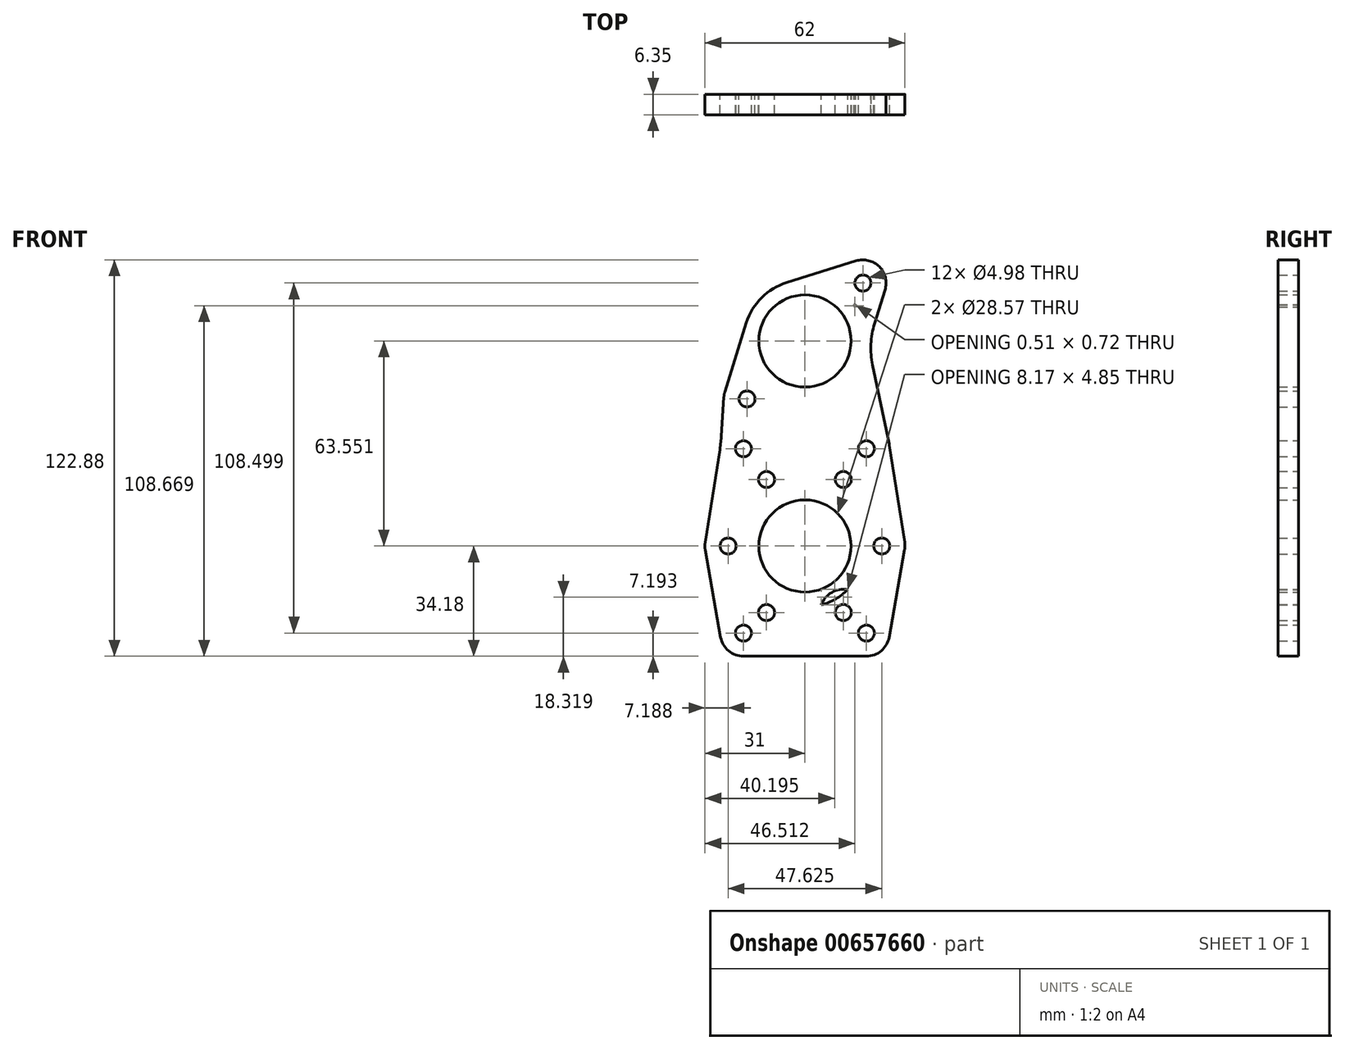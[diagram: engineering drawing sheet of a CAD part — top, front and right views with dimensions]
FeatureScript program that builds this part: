
annotation { "Feature Type Name" : "Feature", "Feature Type Description" : "" }
export const myFeature = defineFeature(function(context is Context, id is Id, definition is map)
    precondition{}
    {
        {
            var Q0;
            Q0=qCreatedBy(makeId("Front.planeOp"),FACE);
            var sketch = newSketch(context, id + "F0", { "sketchPlane" : qUnion([Q0])});
            skLineSegment(sketch, "E0.bottom", {"start": v(0, 0) * mm, "end": v(76.2, 0) * mm});
            skLineSegment(sketch, "E0.top", {"start": v(0, 127) * mm, "end": v(76.2, 127) * mm});
            skLineSegment(sketch, "E0.left", {"start": v(0, 0) * mm, "end": v(0, 127) * mm});
            skLineSegment(sketch, "E0.right", {"start": v(76.2, 0) * mm, "end": v(76.2, 127) * mm});
            skCircle(sketch, "E1", {"center": v(38.1, 38.1) * mm, "radius": 14.29 * mm});
            skCircle(sketch, "E2", {"center": v(38.1, 38.1) * mm, "radius": 23.81 * mm, "construction": true});
            skLineSegment(sketch, "E3", {"start": v(38.1, 38.1) * mm, "end": v(14.29, 38.1) * mm});
            skCircle(sketch, "E4", {"center": v(14.29, 38.1) * mm, "radius": 2.49 * mm});
            skCircle(sketch, "E5.1.0", {"center": v(26.2, 17.48) * mm, "radius": 2.49 * mm});
            skCircle(sketch, "E5.2.0", {"center": v(50, 17.48) * mm, "radius": 2.49 * mm});
            skCircle(sketch, "E5.3.0", {"center": v(61.91, 38.1) * mm, "radius": 2.49 * mm});
            skCircle(sketch, "E5.4.0", {"center": v(50, 58.72) * mm, "radius": 2.49 * mm});
            skCircle(sketch, "E5.5.0", {"center": v(26.2, 58.72) * mm, "radius": 2.49 * mm});
            skLineSegment(sketch, "E6.bottom", {"start": v(19.05, 68.26) * mm, "end": v(57.15, 68.26) * mm, "construction": true});
            skLineSegment(sketch, "E6.top", {"start": v(19.05, 11.11) * mm, "end": v(57.15, 11.11) * mm, "construction": true});
            skLineSegment(sketch, "E6.left", {"start": v(19.05, 68.26) * mm, "end": v(19.05, 11.11) * mm, "construction": true});
            skLineSegment(sketch, "E6.right", {"start": v(57.15, 68.26) * mm, "end": v(57.15, 11.11) * mm, "construction": true});
            skCircle(sketch, "E7", {"center": v(19.05, 68.26) * mm, "radius": 2.49 * mm});
            skCircle(sketch, "E8", {"center": v(57.15, 68.26) * mm, "radius": 2.49 * mm});
            skCircle(sketch, "E9", {"center": v(57.15, 11.11) * mm, "radius": 2.49 * mm});
            skCircle(sketch, "E10", {"center": v(19.05, 11.11) * mm, "radius": 2.49 * mm});
            skCircle(sketch, "E11", {"center": v(38.1, 101.65) * mm, "radius": 14.29 * mm});
            skCircle(sketch, "E12", {"center": v(38.1, 101.65) * mm, "radius": 25.4 * mm, "construction": true});
            skCircle(sketch, "E13", {"center": v(56.06, 119.61) * mm, "radius": 2.49 * mm});
            skLineSegment(sketch, "E14", {"start": v(38.1, 101.65) * mm, "end": v(56.06, 119.61) * mm});
            skLineSegment(sketch, "E15", {"start": v(38.1, 101.65) * mm, "end": v(63.5, 101.65) * mm});
            skCircle(sketch, "E16.1.0", {"center": v(20.14, 83.7) * mm, "radius": 2.49 * mm});
            skLineSegment(sketch, "E16.1.1", {"start": v(76.2, 203.3) * mm, "end": v(76.2, 76.3) * mm});
            skCircle(sketch, "E17", {"center": v(19.05, 11.11) * mm, "radius": 7.19 * mm});
            skCircle(sketch, "E18", {"center": v(57.15, 11.11) * mm, "radius": 7.19 * mm});
            skCircle(sketch, "E19", {"center": v(57.15, 68.26) * mm, "radius": 7.19 * mm});
            skCircle(sketch, "E20", {"center": v(19.05, 68.26) * mm, "radius": 7.19 * mm});
            skCircle(sketch, "E21", {"center": v(14.29, 38.1) * mm, "radius": 7.19 * mm});
            skCircle(sketch, "E22", {"center": v(61.91, 38.1) * mm, "radius": 7.19 * mm});
            skCircle(sketch, "E23", {"center": v(38.1, 38.1) * mm, "radius": 18.99 * mm});
            skLineSegment(sketch, "E24", {"start": v(15.67, 61.92) * mm, "end": v(20.31, 61.19) * mm, "construction": true});
            skLineSegment(sketch, "E25", {"start": v(20.31, 61.19) * mm, "end": v(17.67, 44.44) * mm});
            skLineSegment(sketch, "E26", {"start": v(15.67, 61.92) * mm, "end": v(13.03, 45.18) * mm});
            skLineSegment(sketch, "E27", {"start": v(55.89, 61.19) * mm, "end": v(58.53, 44.44) * mm});
            skLineSegment(sketch, "E28", {"start": v(58.53, 44.44) * mm, "end": v(63.17, 45.18) * mm, "construction": true});
            skLineSegment(sketch, "E29", {"start": v(63.17, 45.18) * mm, "end": v(60.53, 61.92) * mm});
            skLineSegment(sketch, "E30", {"start": v(25.84, 13.46) * mm, "end": v(50.36, 13.46) * mm});
            skLineSegment(sketch, "E31", {"start": v(25.84, 8.76) * mm, "end": v(50.36, 8.76) * mm});
            skCircle(sketch, "E32", {"center": v(26.2, 17.48) * mm, "radius": 7.19 * mm});
            skCircle(sketch, "E33", {"center": v(50, 17.48) * mm, "radius": 7.19 * mm});
            skCircle(sketch, "E34", {"center": v(26.2, 58.72) * mm, "radius": 7.19 * mm});
            skCircle(sketch, "E35", {"center": v(50, 58.72) * mm, "radius": 7.19 * mm});
            skLineSegment(sketch, "E36", {"start": v(15.56, 17.4) * mm, "end": v(13.15, 31) * mm});
            skLineSegment(sketch, "E37", {"start": v(13.15, 31) * mm, "end": v(17.78, 31.82) * mm, "construction": true});
            skLineSegment(sketch, "E38", {"start": v(17.78, 31.82) * mm, "end": v(20.18, 18.21) * mm});
            skLineSegment(sketch, "E39", {"start": v(63.05, 31) * mm, "end": v(60.64, 17.4) * mm});
            skLineSegment(sketch, "E40", {"start": v(60.64, 17.4) * mm, "end": v(56.02, 18.21) * mm, "construction": true});
            skLineSegment(sketch, "E41", {"start": v(56.02, 18.21) * mm, "end": v(58.42, 31.82) * mm});
            skCircle(sketch, "E42", {"center": v(38.1, 101.65) * mm, "radius": 18.99 * mm});
            skCircle(sketch, "E43", {"center": v(20.14, 83.7) * mm, "radius": 7.19 * mm});
            skCircle(sketch, "E44", {"center": v(56.06, 119.61) * mm, "radius": 7.19 * mm});
            skLineSegment(sketch, "E45", {"start": v(17.32, 77.08) * mm, "end": v(22, 76.75) * mm, "construction": true});
            skLineSegment(sketch, "E46", {"start": v(22, 76.75) * mm, "end": v(21.87, 74.87) * mm});
            skLineSegment(sketch, "E47", {"start": v(17.32, 77.08) * mm, "end": v(17.18, 75.2) * mm});
            skLineSegment(sketch, "E48", {"start": v(35.75, 56.94) * mm, "end": v(40.45, 56.94) * mm, "construction": true});
            skLineSegment(sketch, "E49", {"start": v(40.45, 56.94) * mm, "end": v(40.45, 82.81) * mm});
            skLineSegment(sketch, "E50", {"start": v(35.75, 56.94) * mm, "end": v(35.75, 82.81) * mm});
            skLineSegment(sketch, "E51", {"start": v(51.74, 73) * mm, "end": v(45.4, 84.12) * mm});
            skLineSegment(sketch, "E52", {"start": v(45.4, 84.12) * mm, "end": v(49.48, 86.45) * mm, "construction": true});
            skLineSegment(sketch, "E53", {"start": v(49.48, 86.45) * mm, "end": v(55.82, 75.33) * mm});
            skLineSegment(sketch, "E54", {"start": v(59.35, 75.1) * mm, "end": v(58.55, 112.87) * mm});
            skLineSegment(sketch, "E55", {"start": v(58.55, 112.87) * mm, "end": v(53.86, 112.77) * mm, "construction": true});
            skLineSegment(sketch, "E56", {"start": v(53.86, 112.77) * mm, "end": v(54.66, 75) * mm});
            skLineSegment(sketch, "E57", {"start": v(32.45, 119.78) * mm, "end": v(53.92, 126.47) * mm});
            skLineSegment(sketch, "E58", {"start": v(19.97, 107.3) * mm, "end": v(13.28, 85.83) * mm});
            skLineSegment(sketch, "E59", {"start": v(12.97, 84.2) * mm, "end": v(11.88, 68.77) * mm});
            skLineSegment(sketch, "E60", {"start": v(11.95, 69.38) * mm, "end": v(7.19, 39.22) * mm});
            skLineSegment(sketch, "E61", {"start": v(7.2, 36.85) * mm, "end": v(11.97, 9.86) * mm});
            skLineSegment(sketch, "E62", {"start": v(19.05, 3.92) * mm, "end": v(57.15, 3.92) * mm});
            skLineSegment(sketch, "E63", {"start": v(64.23, 9.86) * mm, "end": v(69, 36.85) * mm});
            skLineSegment(sketch, "E64", {"start": v(69.01, 39.22) * mm, "end": v(64.25, 69.38) * mm});
            skLineSegment(sketch, "E65", {"start": v(64.19, 69.74) * mm, "end": v(56.68, 105.54) * mm});
            skLineSegment(sketch, "E66", {"start": v(56.23, 96) * mm, "end": v(62.92, 117.47) * mm});
            skSolve(sketch);
        }
        {
            var Q0;
            Q0=makeQuery(id+"F0.imprint","IMPRINT",FACE,{"disambiguationData":[TD([[makeQuery(id+"F0.imprint","IMPRINT",EDGE,{"derivedFrom":sQuery(id+"F0.wireOp",EDGE,"E16.1.0")}),-1.0]])]});
            var Q1;
            {var subQ7=sQuery(id+"F0.wireOp",EDGE,"E11");var subQ9=sQuery(id+"F0.wireOp",EDGE,"E14");var subQ10=makeQuery(id+"F0.imprint","INTERSECT",VERTEX,{"derivedFrom":[subQ7,subQ9]});Q1=makeQuery(id+"F0.imprint","IMPRINT",FACE,{"disambiguationData":[TD([[makeQuery(id+"F0.imprint","IMPRINT",EDGE,{"disambiguationData":[TD([[subQ10,-1.0]])],"derivedFrom":subQ7}),-1.0]])]});}
            var Q2;
            {var subQ0=sQuery(id+"F0.wireOp",EDGE,"E43");var subQ1=sQuery(id+"F0.wireOp",EDGE,"E42");var subQ2=makeQuery(id+"F0.imprint","INTERSECT",VERTEX,{"disambiguationData":[OD(0.0)],"derivedFrom":[subQ1,subQ0]});Q2=makeQuery(id+"F0.imprint","IMPRINT",FACE,{"disambiguationData":[TD([[makeQuery(id+"F0.imprint","IMPRINT",EDGE,{"disambiguationData":[TD([[subQ2,-1.0]])],"derivedFrom":subQ1}),1.0]])]});}
            var Q3;
            {var subQ3=sQuery(id+"F0.wireOp",EDGE,"E11");var subQ7=sQuery(id+"F0.wireOp",EDGE,"E14");var subQ9=makeQuery(id+"F0.imprint","INTERSECT",VERTEX,{"derivedFrom":[subQ3,subQ7]});Q3=makeQuery(id+"F0.imprint","IMPRINT",FACE,{"disambiguationData":[TD([[makeQuery(id+"F0.imprint","IMPRINT",EDGE,{"disambiguationData":[TD([[subQ9,1.0]])],"derivedFrom":subQ3}),-1.0]])]});}
            var Q4;
            {var subQ0=sQuery(id+"F0.wireOp",EDGE,"E42");var subQ1=sQuery(id+"F0.wireOp",EDGE,"E14");var subQ2=makeQuery(id+"F0.imprint","INTERSECT",VERTEX,{"derivedFrom":[subQ1,subQ0]});Q4=makeQuery(id+"F0.imprint","IMPRINT",FACE,{"disambiguationData":[TD([[makeQuery(id+"F0.imprint","IMPRINT",EDGE,{"disambiguationData":[TD([[subQ2,1.0]])],"derivedFrom":subQ1}),1.0]])]});}
            var Q5;
            {var subQ0=sQuery(id+"F0.wireOp",EDGE,"E42");var subQ1=sQuery(id+"F0.wireOp",EDGE,"E14");var subQ2=makeQuery(id+"F0.imprint","INTERSECT",VERTEX,{"derivedFrom":[subQ1,subQ0]});Q5=makeQuery(id+"F0.imprint","IMPRINT",FACE,{"disambiguationData":[TD([[makeQuery(id+"F0.imprint","IMPRINT",EDGE,{"disambiguationData":[TD([[subQ2,1.0]])],"derivedFrom":subQ1}),-1.0]])]});}
            var Q6;
            Q6=makeQuery(id+"F0.imprint","IMPRINT",FACE,{"disambiguationData":[TD([[makeQuery(id+"F0.imprint","IMPRINT",EDGE,{"derivedFrom":sQuery(id+"F0.wireOp",EDGE,"E13")}),-1.0]])]});
            var Q7;
            {var subQ0=sQuery(id+"F0.wireOp",EDGE,"E46");Q7=makeQuery(id+"F0.imprint","IMPRINT",FACE,{"disambiguationData":[TD([[makeQuery(id+"F0.imprint","IMPRINT",EDGE,{"derivedFrom":subQ0}),-1.0]])]});}
            var Q8;
            Q8=makeQuery(id+"F0.imprint","IMPRINT",FACE,{"disambiguationData":[TD([[makeQuery(id+"F0.imprint","IMPRINT",EDGE,{"derivedFrom":sQuery(id+"F0.wireOp",EDGE,"E7")}),-1.0]])]});
            var Q9;
            {var subQ0=sQuery(id+"F0.wireOp",EDGE,"E20");var subQ1=makeQuery(id+"F0.imprint","INTERSECT",VERTEX,{"derivedFrom":[subQ0,sQuery(id+"F0.wireOp",EDGE,"E25")]});Q9=makeQuery(id+"F0.imprint","IMPRINT",FACE,{"disambiguationData":[TD([[makeQuery(id+"F0.imprint","IMPRINT",EDGE,{"disambiguationData":[TD([[subQ1,1.0]])],"derivedFrom":subQ0}),1.0]])]});}
            var Q10;
            Q10=makeQuery(id+"F0.imprint","IMPRINT",FACE,{"disambiguationData":[TD([[makeQuery(id+"F0.imprint","IMPRINT",EDGE,{"derivedFrom":sQuery(id+"F0.wireOp",EDGE,"E5.5.0")}),-1.0]])]});
            var Q11;
            Q11=makeQuery(id+"F0.imprint","IMPRINT",FACE,{"disambiguationData":[TD([[makeQuery(id+"F0.imprint","IMPRINT",EDGE,{"derivedFrom":sQuery(id+"F0.wireOp",EDGE,"E8")}),-1.0]])]});
            var Q12;
            {var subQ0=sQuery(id+"F0.wireOp",EDGE,"E29");Q12=makeQuery(id+"F0.imprint","IMPRINT",FACE,{"disambiguationData":[TD([[makeQuery(id+"F0.imprint","IMPRINT",EDGE,{"derivedFrom":subQ0}),1.0]])]});}
            var Q13;
            Q13=makeQuery(id+"F0.imprint","IMPRINT",FACE,{"disambiguationData":[TD([[makeQuery(id+"F0.imprint","IMPRINT",EDGE,{"derivedFrom":sQuery(id+"F0.wireOp",EDGE,"E5.3.0")}),-1.0]])]});
            var Q14;
            Q14=makeQuery(id+"F0.imprint","IMPRINT",FACE,{"disambiguationData":[TD([[makeQuery(id+"F0.imprint","IMPRINT",EDGE,{"derivedFrom":sQuery(id+"F0.wireOp",EDGE,"E5.4.0")}),-1.0]])]});
            var Q15;
            Q15=makeQuery(id+"F0.imprint","IMPRINT",FACE,{"disambiguationData":[TD([[makeQuery(id+"F0.imprint","IMPRINT",EDGE,{"derivedFrom":sQuery(id+"F0.wireOp",EDGE,"E1")}),-1.0]])]});
            var Q16;
            {var subQ0=sQuery(id+"F0.wireOp",EDGE,"E19");var subQ1=makeQuery(id+"F0.imprint","INTERSECT",VERTEX,{"derivedFrom":[subQ0,sQuery(id+"F0.wireOp",EDGE,"E27")]});Q16=makeQuery(id+"F0.imprint","IMPRINT",FACE,{"disambiguationData":[TD([[makeQuery(id+"F0.imprint","IMPRINT",EDGE,{"disambiguationData":[TD([[subQ1,1.0]])],"derivedFrom":subQ0}),1.0]])]});}
            var Q17;
            {var subQ0=sQuery(id+"F0.wireOp",EDGE,"E27");var subQ1=sQuery(id+"F0.wireOp",EDGE,"E19");var subQ2=makeQuery(id+"F0.imprint","INTERSECT",VERTEX,{"derivedFrom":[subQ1,subQ0]});Q17=makeQuery(id+"F0.imprint","IMPRINT",FACE,{"disambiguationData":[TD([[makeQuery(id+"F0.imprint","IMPRINT",EDGE,{"disambiguationData":[TD([[subQ2,-1.0]])],"derivedFrom":subQ1}),-1.0]])]});}
            var Q18;
            {var subQ0=sQuery(id+"F0.wireOp",EDGE,"E34");var subQ1=sQuery(id+"F0.wireOp",EDGE,"E23");var subQ2=makeQuery(id+"F0.imprint","INTERSECT",VERTEX,{"disambiguationData":[OD(0.0)],"derivedFrom":[subQ1,subQ0]});Q18=makeQuery(id+"F0.imprint","IMPRINT",FACE,{"disambiguationData":[TD([[makeQuery(id+"F0.imprint","IMPRINT",EDGE,{"disambiguationData":[TD([[subQ2,-1.0]])],"derivedFrom":subQ1}),1.0]])]});}
            var Q19;
            {var subQ0=sQuery(id+"F0.wireOp",EDGE,"E26");Q19=makeQuery(id+"F0.imprint","IMPRINT",FACE,{"disambiguationData":[TD([[makeQuery(id+"F0.imprint","IMPRINT",EDGE,{"derivedFrom":subQ0}),1.0]])]});}
            var Q20;
            {var subQ0=sQuery(id+"F0.wireOp",EDGE,"E25");var subQ1=sQuery(id+"F0.wireOp",EDGE,"E20");var subQ2=makeQuery(id+"F0.imprint","INTERSECT",VERTEX,{"derivedFrom":[subQ1,subQ0]});Q20=makeQuery(id+"F0.imprint","IMPRINT",FACE,{"disambiguationData":[TD([[makeQuery(id+"F0.imprint","IMPRINT",EDGE,{"disambiguationData":[TD([[subQ2,1.0]])],"derivedFrom":subQ1}),-1.0]])]});}
            var Q21;
            {var subQ0=sQuery(id+"F0.wireOp",EDGE,"E35");var subQ1=sQuery(id+"F0.wireOp",EDGE,"E23");var subQ2=makeQuery(id+"F0.imprint","INTERSECT",VERTEX,{"disambiguationData":[OD(0.0)],"derivedFrom":[subQ1,subQ0]});Q21=makeQuery(id+"F0.imprint","IMPRINT",FACE,{"disambiguationData":[TD([[makeQuery(id+"F0.imprint","IMPRINT",EDGE,{"disambiguationData":[TD([[subQ2,-1.0]])],"derivedFrom":subQ1}),1.0]])]});}
            var Q22;
            {var subQ0=sQuery(id+"F0.wireOp",EDGE,"E23");var subQ1=sQuery(id+"F0.wireOp",EDGE,"E22");var subQ2=makeQuery(id+"F0.imprint","INTERSECT",VERTEX,{"disambiguationData":[OD(0.0)],"derivedFrom":[subQ1,subQ0]});Q22=makeQuery(id+"F0.imprint","IMPRINT",FACE,{"disambiguationData":[TD([[makeQuery(id+"F0.imprint","IMPRINT",EDGE,{"disambiguationData":[TD([[subQ2,-1.0]])],"derivedFrom":subQ1}),1.0]])]});}
            var Q23;
            Q23=makeQuery(id+"F0.imprint","IMPRINT",FACE,{"disambiguationData":[TD([[makeQuery(id+"F0.imprint","IMPRINT",EDGE,{"derivedFrom":sQuery(id+"F0.wireOp",EDGE,"E4")}),-1.0]])]});
            var Q24;
            {var subQ0=sQuery(id+"F0.wireOp",EDGE,"E36");Q24=makeQuery(id+"F0.imprint","IMPRINT",FACE,{"disambiguationData":[TD([[makeQuery(id+"F0.imprint","IMPRINT",EDGE,{"derivedFrom":subQ0}),-1.0]])]});}
            var Q25;
            {var subQ2=sQuery(id+"F0.wireOp",EDGE,"E32");var subQ6=sQuery(id+"F0.wireOp",EDGE,"E10");var subQ7=makeQuery(id+"F0.imprint","INTERSECT",VERTEX,{"disambiguationData":[OD(0.0)],"derivedFrom":[subQ6,subQ2]});Q25=makeQuery(id+"F0.imprint","IMPRINT",FACE,{"disambiguationData":[TD([[makeQuery(id+"F0.imprint","IMPRINT",EDGE,{"disambiguationData":[TD([[subQ7,-1.0]])],"derivedFrom":subQ6}),-1.0]])]});}
            var Q26;
            {var subQ0=sQuery(id+"F0.wireOp",EDGE,"E21");var subQ1=sQuery(id+"F0.wireOp",EDGE,"E3");var subQ2=makeQuery(id+"F0.imprint","INTERSECT",VERTEX,{"derivedFrom":[subQ1,subQ0]});Q26=makeQuery(id+"F0.imprint","IMPRINT",FACE,{"disambiguationData":[TD([[makeQuery(id+"F0.imprint","IMPRINT",EDGE,{"disambiguationData":[TD([[subQ2,-1.0]])],"derivedFrom":subQ1}),-1.0]])]});}
            var Q27;
            {var subQ0=sQuery(id+"F0.wireOp",EDGE,"E32");var subQ1=sQuery(id+"F0.wireOp",EDGE,"E23");var subQ2=makeQuery(id+"F0.imprint","INTERSECT",VERTEX,{"disambiguationData":[OD(0.0)],"derivedFrom":[subQ1,subQ0]});Q27=makeQuery(id+"F0.imprint","IMPRINT",FACE,{"disambiguationData":[TD([[makeQuery(id+"F0.imprint","IMPRINT",EDGE,{"disambiguationData":[TD([[subQ2,-1.0]])],"derivedFrom":subQ1}),1.0]])]});}
            var Q28;
            {var subQ0=sQuery(id+"F0.wireOp",EDGE,"E17");var subQ2=sQuery(id+"F0.wireOp",EDGE,"E5.1.0");var subQ3=makeQuery(id+"F0.imprint","INTERSECT",VERTEX,{"disambiguationData":[OD(0.0)],"derivedFrom":[subQ2,subQ0]});Q28=makeQuery(id+"F0.imprint","IMPRINT",FACE,{"disambiguationData":[TD([[makeQuery(id+"F0.imprint","IMPRINT",EDGE,{"disambiguationData":[TD([[subQ3,1.0]])],"derivedFrom":subQ2}),-1.0]])]});}
            var Q29;
            {var subQ0=sQuery(id+"F0.wireOp",EDGE,"E30");var subQ1=sQuery(id+"F0.wireOp",EDGE,"E17");var subQ2=makeQuery(id+"F0.imprint","INTERSECT",VERTEX,{"derivedFrom":[subQ1,subQ0]});Q29=makeQuery(id+"F0.imprint","IMPRINT",FACE,{"disambiguationData":[TD([[makeQuery(id+"F0.imprint","IMPRINT",EDGE,{"disambiguationData":[TD([[subQ2,1.0]])],"derivedFrom":subQ1}),-1.0]])]});}
            var Q30;
            {var subQ0=sQuery(id+"F0.wireOp",EDGE,"E38");var subQ1=sQuery(id+"F0.wireOp",EDGE,"E17");var subQ2=makeQuery(id+"F0.imprint","INTERSECT",VERTEX,{"derivedFrom":[subQ1,subQ0]});Q30=makeQuery(id+"F0.imprint","IMPRINT",FACE,{"disambiguationData":[TD([[makeQuery(id+"F0.imprint","IMPRINT",EDGE,{"disambiguationData":[TD([[subQ2,-1.0]])],"derivedFrom":subQ1}),-1.0]])]});}
            var Q31;
            {var subQ0=sQuery(id+"F0.wireOp",EDGE,"E33");var subQ1=sQuery(id+"F0.wireOp",EDGE,"E23");var subQ2=makeQuery(id+"F0.imprint","INTERSECT",VERTEX,{"disambiguationData":[OD(0.0)],"derivedFrom":[subQ1,subQ0]});Q31=makeQuery(id+"F0.imprint","IMPRINT",FACE,{"disambiguationData":[TD([[makeQuery(id+"F0.imprint","IMPRINT",EDGE,{"disambiguationData":[TD([[subQ2,-1.0]])],"derivedFrom":subQ1}),1.0]])]});}
            var Q32;
            {var subQ5=sQuery(id+"F0.wireOp",EDGE,"E18");var subQ10=sQuery(id+"F0.wireOp",EDGE,"E5.2.0");var subQ13=makeQuery(id+"F0.imprint","INTERSECT",VERTEX,{"disambiguationData":[OD(0.0)],"derivedFrom":[subQ10,subQ5]});Q32=makeQuery(id+"F0.imprint","IMPRINT",FACE,{"disambiguationData":[TD([[makeQuery(id+"F0.imprint","IMPRINT",EDGE,{"disambiguationData":[TD([[subQ13,-1.0]])],"derivedFrom":subQ10}),-1.0]])]});}
            var Q33;
            {var subQ0=sQuery(id+"F0.wireOp",EDGE,"E39");Q33=makeQuery(id+"F0.imprint","IMPRINT",FACE,{"disambiguationData":[TD([[makeQuery(id+"F0.imprint","IMPRINT",EDGE,{"derivedFrom":subQ0}),-1.0]])]});}
            var Q34;
            {var subQ0=sQuery(id+"F0.wireOp",EDGE,"E41");var subQ1=sQuery(id+"F0.wireOp",EDGE,"E18");var subQ2=makeQuery(id+"F0.imprint","INTERSECT",VERTEX,{"derivedFrom":[subQ1,subQ0]});Q34=makeQuery(id+"F0.imprint","IMPRINT",FACE,{"disambiguationData":[TD([[makeQuery(id+"F0.imprint","IMPRINT",EDGE,{"disambiguationData":[TD([[subQ2,1.0]])],"derivedFrom":subQ1}),-1.0]])]});}
            var Q35;
            {var subQ0=sQuery(id+"F0.wireOp",EDGE,"E18");var subQ2=sQuery(id+"F0.wireOp",EDGE,"E5.2.0");var subQ3=makeQuery(id+"F0.imprint","INTERSECT",VERTEX,{"disambiguationData":[OD(0.0)],"derivedFrom":[subQ2,subQ0]});Q35=makeQuery(id+"F0.imprint","IMPRINT",FACE,{"disambiguationData":[TD([[makeQuery(id+"F0.imprint","IMPRINT",EDGE,{"disambiguationData":[TD([[subQ3,1.0]])],"derivedFrom":subQ2}),-1.0]])]});}
            var Q36;
            {var subQ0=sQuery(id+"F0.wireOp",EDGE,"E30");var subQ1=sQuery(id+"F0.wireOp",EDGE,"E18");var subQ2=makeQuery(id+"F0.imprint","INTERSECT",VERTEX,{"derivedFrom":[subQ1,subQ0]});Q36=makeQuery(id+"F0.imprint","IMPRINT",FACE,{"disambiguationData":[TD([[makeQuery(id+"F0.imprint","IMPRINT",EDGE,{"disambiguationData":[TD([[subQ2,-1.0]])],"derivedFrom":subQ1}),-1.0]])]});}
            var Q37;
            {var subQ5=sQuery(id+"F0.wireOp",EDGE,"E17");var subQ10=sQuery(id+"F0.wireOp",EDGE,"E5.1.0");var subQ13=makeQuery(id+"F0.imprint","INTERSECT",VERTEX,{"disambiguationData":[OD(0.0)],"derivedFrom":[subQ10,subQ5]});Q37=makeQuery(id+"F0.imprint","IMPRINT",FACE,{"disambiguationData":[TD([[makeQuery(id+"F0.imprint","IMPRINT",EDGE,{"disambiguationData":[TD([[subQ13,-1.0]])],"derivedFrom":subQ10}),-1.0]])]});}
            var Q38;
            {var subQ0=sQuery(id+"F0.wireOp",EDGE,"E21");var subQ1=sQuery(id+"F0.wireOp",EDGE,"E3");var subQ2=makeQuery(id+"F0.imprint","INTERSECT",VERTEX,{"derivedFrom":[subQ1,subQ0]});Q38=makeQuery(id+"F0.imprint","IMPRINT",FACE,{"disambiguationData":[TD([[makeQuery(id+"F0.imprint","IMPRINT",EDGE,{"disambiguationData":[TD([[subQ2,-1.0]])],"derivedFrom":subQ1}),1.0]])]});}
            var Q39;
            {var subQ3=sQuery(id+"F0.wireOp",EDGE,"E33");var subQ6=sQuery(id+"F0.wireOp",EDGE,"E9");var subQ7=makeQuery(id+"F0.imprint","INTERSECT",VERTEX,{"disambiguationData":[OD(0.0)],"derivedFrom":[subQ6,subQ3]});Q39=makeQuery(id+"F0.imprint","IMPRINT",FACE,{"disambiguationData":[TD([[makeQuery(id+"F0.imprint","IMPRINT",EDGE,{"disambiguationData":[TD([[subQ7,-1.0]])],"derivedFrom":subQ6}),-1.0]])]});}
            var Q40;
            {var subQ5=sQuery(id+"F0.wireOp",EDGE,"E31");Q40=makeQuery(id+"F0.imprint","IMPRINT",FACE,{"disambiguationData":[TD([[makeQuery(id+"F0.imprint","IMPRINT",EDGE,{"derivedFrom":subQ5}),1.0]])]});}
            var Q41;
            {var subQ0=sQuery(id+"F0.wireOp",EDGE,"E56");var subQ1=sQuery(id+"F0.wireOp",EDGE,"E15");var subQ2=makeQuery(id+"F0.imprint","INTERSECT",VERTEX,{"derivedFrom":[subQ1,subQ0]});Q41=makeQuery(id+"F0.imprint","IMPRINT",FACE,{"disambiguationData":[TD([[makeQuery(id+"F0.imprint","IMPRINT",EDGE,{"disambiguationData":[TD([[subQ2,-1.0]])],"derivedFrom":subQ1}),1.0]])]});}
            var Q42;
            {var subQ0=sQuery(id+"F0.wireOp",EDGE,"E56");var subQ1=sQuery(id+"F0.wireOp",EDGE,"E42");var subQ2=makeQuery(id+"F0.imprint","INTERSECT",VERTEX,{"disambiguationData":[OD(0.0)],"derivedFrom":[subQ1,subQ0]});Q42=makeQuery(id+"F0.imprint","IMPRINT",FACE,{"disambiguationData":[TD([[makeQuery(id+"F0.imprint","IMPRINT",EDGE,{"disambiguationData":[TD([[subQ2,-1.0]])],"derivedFrom":subQ1}),-1.0]])]});}
            var Q43;
            {var subQ0=sQuery(id+"F0.wireOp",EDGE,"E49");Q43=makeQuery(id+"F0.imprint","IMPRINT",FACE,{"disambiguationData":[TD([[makeQuery(id+"F0.imprint","IMPRINT",EDGE,{"derivedFrom":subQ0}),1.0]])]});}
            var Q44;
            {var subQ5=sQuery(id+"F0.wireOp",EDGE,"E51");Q44=makeQuery(id+"F0.imprint","IMPRINT",FACE,{"disambiguationData":[TD([[makeQuery(id+"F0.imprint","IMPRINT",EDGE,{"derivedFrom":subQ5}),-1.0]])]});}
            var Q45;
            {var subQ0=sQuery(id+"F0.wireOp",EDGE,"E53");var subQ1=sQuery(id+"F0.wireOp",EDGE,"E19");var subQ2=makeQuery(id+"F0.imprint","INTERSECT",VERTEX,{"derivedFrom":[subQ1,subQ0]});Q45=makeQuery(id+"F0.imprint","IMPRINT",FACE,{"disambiguationData":[TD([[makeQuery(id+"F0.imprint","IMPRINT",EDGE,{"disambiguationData":[TD([[subQ2,-1.0]])],"derivedFrom":subQ1}),-1.0]])]});}
            var Q46;
            {var subQ0=sQuery(id+"F0.wireOp",EDGE,"E56");var subQ1=sQuery(id+"F0.wireOp",EDGE,"E15");var subQ2=makeQuery(id+"F0.imprint","INTERSECT",VERTEX,{"derivedFrom":[subQ1,subQ0]});Q46=makeQuery(id+"F0.imprint","IMPRINT",FACE,{"disambiguationData":[TD([[makeQuery(id+"F0.imprint","IMPRINT",EDGE,{"disambiguationData":[TD([[subQ2,-1.0]])],"derivedFrom":subQ1}),-1.0]])]});}
            var Q47;
            {var subQ0=sQuery(id+"F0.wireOp",EDGE,"E57");Q47=makeQuery(id+"F0.imprint","IMPRINT",FACE,{"disambiguationData":[TD([[makeQuery(id+"F0.imprint","IMPRINT",EDGE,{"derivedFrom":subQ0}),-1.0]])]});}
            var Q48;
            {var subQ0=sQuery(id+"F0.wireOp",EDGE,"E58");Q48=makeQuery(id+"F0.imprint","IMPRINT",FACE,{"disambiguationData":[TD([[makeQuery(id+"F0.imprint","IMPRINT",EDGE,{"derivedFrom":subQ0}),1.0]])]});}
            var Q49;
            {var subQ5=sQuery(id+"F0.wireOp",EDGE,"E47");Q49=makeQuery(id+"F0.imprint","IMPRINT",FACE,{"disambiguationData":[TD([[makeQuery(id+"F0.imprint","IMPRINT",EDGE,{"derivedFrom":subQ5}),-1.0]])]});}
            var Q50;
            {var subQ5=sQuery(id+"F0.wireOp",EDGE,"E26");Q50=makeQuery(id+"F0.imprint","IMPRINT",FACE,{"disambiguationData":[TD([[makeQuery(id+"F0.imprint","IMPRINT",EDGE,{"derivedFrom":subQ5}),-1.0]])]});}
            var Q51;
            {var subQ0=sQuery(id+"F0.wireOp",EDGE,"E31");Q51=makeQuery(id+"F0.imprint","IMPRINT",FACE,{"disambiguationData":[TD([[makeQuery(id+"F0.imprint","IMPRINT",EDGE,{"derivedFrom":subQ0}),-1.0]])]});}
            var Q52;
            {var subQ0=sQuery(id+"F0.wireOp",EDGE,"E39");Q52=makeQuery(id+"F0.imprint","IMPRINT",FACE,{"disambiguationData":[TD([[makeQuery(id+"F0.imprint","IMPRINT",EDGE,{"derivedFrom":subQ0}),1.0]])]});}
            var Q53;
            {var subQ0=sQuery(id+"F0.wireOp",EDGE,"E29");Q53=makeQuery(id+"F0.imprint","IMPRINT",FACE,{"disambiguationData":[TD([[makeQuery(id+"F0.imprint","IMPRINT",EDGE,{"derivedFrom":subQ0}),-1.0]])]});}
            var Q54;
            {var subQ0=sQuery(id+"F0.wireOp",EDGE,"E54");var subQ1=sQuery(id+"F0.wireOp",EDGE,"E19");var subQ2=makeQuery(id+"F0.imprint","INTERSECT",VERTEX,{"derivedFrom":[subQ1,subQ0]});Q54=makeQuery(id+"F0.imprint","IMPRINT",FACE,{"disambiguationData":[TD([[makeQuery(id+"F0.imprint","IMPRINT",EDGE,{"disambiguationData":[TD([[subQ2,1.0]])],"derivedFrom":subQ1}),-1.0]])]});}
            var Q55;
            {var subQ0=sQuery(id+"F0.wireOp",EDGE,"E54");var subQ1=sQuery(id+"F0.wireOp",EDGE,"E44");var subQ2=makeQuery(id+"F0.imprint","INTERSECT",VERTEX,{"derivedFrom":[subQ1,subQ0]});Q55=makeQuery(id+"F0.imprint","IMPRINT",FACE,{"disambiguationData":[TD([[makeQuery(id+"F0.imprint","IMPRINT",EDGE,{"disambiguationData":[TD([[subQ2,-1.0]])],"derivedFrom":subQ1}),-1.0]])]});}
            var Q56;
            {var subQ5=sQuery(id+"F0.wireOp",EDGE,"E65");var subQ11=sQuery(id+"F0.wireOp",EDGE,"E15");var subQ13=makeQuery(id+"F0.imprint","INTERSECT",VERTEX,{"derivedFrom":[subQ11,subQ5]});Q56=makeQuery(id+"F0.imprint","IMPRINT",FACE,{"disambiguationData":[TD([[makeQuery(id+"F0.imprint","IMPRINT",EDGE,{"disambiguationData":[TD([[subQ13,-1.0]])],"derivedFrom":subQ11}),1.0]])]});}
            var Q57;
            {var subQ1=sQuery(id+"F0.wireOp",EDGE,"E19");var subQ10=sQuery(id+"F0.wireOp",EDGE,"E53");var subQ11=makeQuery(id+"F0.imprint","INTERSECT",VERTEX,{"derivedFrom":[subQ1,subQ10]});Q57=makeQuery(id+"F0.imprint","IMPRINT",FACE,{"disambiguationData":[TD([[makeQuery(id+"F0.imprint","IMPRINT",EDGE,{"disambiguationData":[TD([[subQ11,1.0]])],"derivedFrom":subQ1}),-1.0]])]});}
            var Q58;
            {var subQ0=sQuery(id+"F0.wireOp",EDGE,"E53");var subQ1=sQuery(id+"F0.wireOp",EDGE,"E42");var subQ2=makeQuery(id+"F0.imprint","INTERSECT",VERTEX,{"derivedFrom":[subQ1,subQ0]});Q58=makeQuery(id+"F0.imprint","IMPRINT",FACE,{"disambiguationData":[TD([[makeQuery(id+"F0.imprint","IMPRINT",EDGE,{"disambiguationData":[TD([[subQ2,-1.0]])],"derivedFrom":subQ1}),-1.0]])]});}
            var Q59;
            {var subQ0=sQuery(id+"F0.wireOp",EDGE,"E49");Q59=makeQuery(id+"F0.imprint","IMPRINT",FACE,{"disambiguationData":[TD([[makeQuery(id+"F0.imprint","IMPRINT",EDGE,{"derivedFrom":subQ0}),-1.0]])]});}
            var Q60;
            {var subQ9=sQuery(id+"F0.wireOp",EDGE,"E46");Q60=makeQuery(id+"F0.imprint","IMPRINT",FACE,{"disambiguationData":[TD([[makeQuery(id+"F0.imprint","IMPRINT",EDGE,{"derivedFrom":subQ9}),1.0]])]});}
            var Q61;
            {var subQ0=sQuery(id+"F0.wireOp",EDGE,"E25");var subQ1=sQuery(id+"F0.wireOp",EDGE,"E21");var subQ2=makeQuery(id+"F0.imprint","INTERSECT",VERTEX,{"derivedFrom":[subQ1,subQ0]});Q61=makeQuery(id+"F0.imprint","IMPRINT",FACE,{"disambiguationData":[TD([[makeQuery(id+"F0.imprint","IMPRINT",EDGE,{"disambiguationData":[TD([[subQ2,1.0]])],"derivedFrom":subQ1}),-1.0]])]});}
            var Q62;
            {var subQ0=sQuery(id+"F0.wireOp",EDGE,"E27");var subQ1=sQuery(id+"F0.wireOp",EDGE,"E22");var subQ2=makeQuery(id+"F0.imprint","INTERSECT",VERTEX,{"derivedFrom":[subQ1,subQ0]});Q62=makeQuery(id+"F0.imprint","IMPRINT",FACE,{"disambiguationData":[TD([[makeQuery(id+"F0.imprint","IMPRINT",EDGE,{"disambiguationData":[TD([[subQ2,-1.0]])],"derivedFrom":subQ1}),-1.0]])]});}
            var Q63;
            {var subQ0=sQuery(id+"F0.wireOp",EDGE,"E41");var subQ1=sQuery(id+"F0.wireOp",EDGE,"E22");var subQ2=makeQuery(id+"F0.imprint","INTERSECT",VERTEX,{"derivedFrom":[subQ1,subQ0]});Q63=makeQuery(id+"F0.imprint","IMPRINT",FACE,{"disambiguationData":[TD([[makeQuery(id+"F0.imprint","IMPRINT",EDGE,{"disambiguationData":[TD([[subQ2,1.0]])],"derivedFrom":subQ1}),-1.0]])]});}
            var Q64;
            {var subQ0=sQuery(id+"F0.wireOp",EDGE,"E32");var subQ1=sQuery(id+"F0.wireOp",EDGE,"E23");var subQ2=makeQuery(id+"F0.imprint","INTERSECT",VERTEX,{"disambiguationData":[OD(1.0)],"derivedFrom":[subQ1,subQ0]});Q64=makeQuery(id+"F0.imprint","IMPRINT",FACE,{"disambiguationData":[TD([[makeQuery(id+"F0.imprint","IMPRINT",EDGE,{"disambiguationData":[TD([[subQ2,-1.0]])],"derivedFrom":subQ1}),-1.0]])]});}
            var Q65;
            {var subQ0=sQuery(id+"F0.wireOp",EDGE,"E38");var subQ1=sQuery(id+"F0.wireOp",EDGE,"E21");var subQ2=makeQuery(id+"F0.imprint","INTERSECT",VERTEX,{"derivedFrom":[subQ1,subQ0]});Q65=makeQuery(id+"F0.imprint","IMPRINT",FACE,{"disambiguationData":[TD([[makeQuery(id+"F0.imprint","IMPRINT",EDGE,{"disambiguationData":[TD([[subQ2,-1.0]])],"derivedFrom":subQ1}),-1.0]])]});}
            var Q66;
            {var subQ0=sQuery(id+"F0.wireOp",EDGE,"E65");var subQ1=sQuery(id+"F0.wireOp",EDGE,"E15");var subQ2=makeQuery(id+"F0.imprint","INTERSECT",VERTEX,{"derivedFrom":[subQ1,subQ0]});Q66=makeQuery(id+"F0.imprint","IMPRINT",FACE,{"disambiguationData":[TD([[makeQuery(id+"F0.imprint","IMPRINT",EDGE,{"disambiguationData":[TD([[subQ2,-1.0]])],"derivedFrom":subQ1}),-1.0]])]});}
            var Q67;
            {var subQ0=sQuery(id+"F0.wireOp",EDGE,"E42");var subQ1=sQuery(id+"F0.wireOp",EDGE,"E15");var subQ2=makeQuery(id+"F0.imprint","INTERSECT",VERTEX,{"derivedFrom":[subQ1,subQ0]});Q67=makeQuery(id+"F0.imprint","IMPRINT",FACE,{"disambiguationData":[TD([[makeQuery(id+"F0.imprint","IMPRINT",EDGE,{"disambiguationData":[TD([[subQ2,-1.0]])],"derivedFrom":subQ1}),-1.0]])]});}
            var Q68;
            {var subQ0=sQuery(id+"F0.wireOp",EDGE,"E42");var subQ1=sQuery(id+"F0.wireOp",EDGE,"E15");var subQ2=makeQuery(id+"F0.imprint","INTERSECT",VERTEX,{"derivedFrom":[subQ1,subQ0]});Q68=makeQuery(id+"F0.imprint","IMPRINT",FACE,{"disambiguationData":[TD([[makeQuery(id+"F0.imprint","IMPRINT",EDGE,{"disambiguationData":[TD([[subQ2,-1.0]])],"derivedFrom":subQ1}),1.0]])]});}
            var Q69;
            {var subQ0=sQuery(id+"F0.wireOp",EDGE,"E36");Q69=makeQuery(id+"F0.imprint","IMPRINT",FACE,{"disambiguationData":[TD([[makeQuery(id+"F0.imprint","IMPRINT",EDGE,{"derivedFrom":subQ0}),1.0]])]});}
            var Q70;
            {var subQ0=sQuery(id+"F0.wireOp",EDGE,"E59");var subQ1=sQuery(id+"F0.wireOp",EDGE,"E20");var subQ2=makeQuery(id+"F0.imprint","INTERSECT",VERTEX,{"derivedFrom":[subQ1,subQ0]});Q70=makeQuery(id+"F0.imprint","IMPRINT",FACE,{"disambiguationData":[TD([[makeQuery(id+"F0.imprint","IMPRINT",EDGE,{"disambiguationData":[TD([[subQ2,1.0]])],"derivedFrom":subQ1}),-1.0]])]});}
            extrude(context, id + "F1", {"entities" : qUnion([Q0, Q1, Q2, Q3, Q4, Q5, Q6, Q7, Q8, Q9, Q10, Q11, Q12, Q13, Q14, Q15, Q16, Q17, Q18, Q19, Q20, Q21, Q22, Q23, Q24, Q25, Q26, Q27, Q28, Q29, Q30, Q31, Q32, Q33, Q34, Q35, Q36, Q37, Q38, Q39, Q40, Q41, Q42, Q43, Q44, Q45, Q46, Q47, Q48, Q49, Q50, Q51, Q52, Q53, Q54, Q55, Q56, Q57, Q58, Q59, Q60, Q61, Q62, Q63, Q64, Q65, Q66, Q67, Q68, Q69, Q70]), "depth" : 6.35 * mm, "offsetDistance" : 25.4 * mm});
        }
        {
            var Q0;
            Q0=makeQuery(id+"F1.opExtrude","SWEPT_EDGE",EDGE,{"disambiguationData":[OSD([sQuery(id+"F0.wireOp",EDGE,"E43"),sQuery(id+"F0.wireOp",EDGE,"E58")])]});
            var Q1;
            Q1=makeQuery(id+"F1.opExtrude","SWEPT_EDGE",EDGE,{"disambiguationData":[OSD([sQuery(id+"F0.wireOp",EDGE,"E43"),sQuery(id+"F0.wireOp",EDGE,"E59")])]});
            var Q2;
            Q2=makeQuery(id+"F1.opExtrude","SWEPT_EDGE",EDGE,{"disambiguationData":[OSD([sQuery(id+"F0.wireOp",EDGE,"E59"),sQuery(id+"F0.wireOp",EDGE,"E60")])]});
            var Q3;
            Q3=makeQuery(id+"F1.opExtrude","SWEPT_EDGE",EDGE,{"disambiguationData":[OSD([sQuery(id+"F0.wireOp",EDGE,"E21"),sQuery(id+"F0.wireOp",EDGE,"E60")])]});
            var Q4;
            Q4=makeQuery(id+"F1.opExtrude","SWEPT_EDGE",EDGE,{"disambiguationData":[OSD([sQuery(id+"F0.wireOp",EDGE,"E21"),sQuery(id+"F0.wireOp",EDGE,"E61")])]});
            var Q5;
            Q5=makeQuery(id+"F1.opExtrude","SWEPT_EDGE",EDGE,{"disambiguationData":[OSD([sQuery(id+"F0.wireOp",EDGE,"E42"),sQuery(id+"F0.wireOp",EDGE,"E58")])]});
            var Q6;
            Q6=makeQuery(id+"F1.opExtrude","SWEPT_EDGE",EDGE,{"disambiguationData":[OSD([sQuery(id+"F0.wireOp",EDGE,"E42"),sQuery(id+"F0.wireOp",EDGE,"E57")])]});
            var Q7;
            Q7=makeQuery(id+"F1.opExtrude","SWEPT_EDGE",EDGE,{"disambiguationData":[OSD([sQuery(id+"F0.wireOp",EDGE,"E17"),sQuery(id+"F0.wireOp",EDGE,"E61")])]});
            var Q8;
            Q8=makeQuery(id+"F1.opExtrude","SWEPT_EDGE",EDGE,{"disambiguationData":[OSD([sQuery(id+"F0.wireOp",EDGE,"E17"),sQuery(id+"F0.wireOp",EDGE,"E62")])]});
            var Q9;
            Q9=makeQuery(id+"F1.opExtrude","SWEPT_EDGE",EDGE,{"disambiguationData":[OSD([sQuery(id+"F0.wireOp",EDGE,"E18"),sQuery(id+"F0.wireOp",EDGE,"E62")])]});
            var Q10;
            Q10=makeQuery(id+"F1.opExtrude","SWEPT_EDGE",EDGE,{"disambiguationData":[OSD([sQuery(id+"F0.wireOp",EDGE,"E18"),sQuery(id+"F0.wireOp",EDGE,"E63")])]});
            var Q11;
            Q11=makeQuery(id+"F1.opExtrude","SWEPT_EDGE",EDGE,{"disambiguationData":[OSD([sQuery(id+"F0.wireOp",EDGE,"E22"),sQuery(id+"F0.wireOp",EDGE,"E64")])]});
            var Q12;
            Q12=makeQuery(id+"F1.opExtrude","SWEPT_EDGE",EDGE,{"disambiguationData":[OSD([sQuery(id+"F0.wireOp",EDGE,"E22"),sQuery(id+"F0.wireOp",EDGE,"E63")])]});
            var Q13;
            Q13=makeQuery(id+"F1.opExtrude","SWEPT_EDGE",EDGE,{"disambiguationData":[OSD([sQuery(id+"F0.wireOp",EDGE,"E19"),sQuery(id+"F0.wireOp",EDGE,"E65")])]});
            var Q14;
            Q14=makeQuery(id+"F1.opExtrude","SWEPT_EDGE",EDGE,{"disambiguationData":[OSD([sQuery(id+"F0.wireOp",EDGE,"E65"),sQuery(id+"F0.wireOp",EDGE,"E66")])]});
            var Q15;
            Q15=makeQuery(id+"F1.opExtrude","SWEPT_EDGE",EDGE,{"disambiguationData":[OSD([sQuery(id+"F0.wireOp",EDGE,"E44"),sQuery(id+"F0.wireOp",EDGE,"E66")])]});
            var Q16;
            Q16=makeQuery(id+"F1.opExtrude","SWEPT_EDGE",EDGE,{"disambiguationData":[OSD([sQuery(id+"F0.wireOp",EDGE,"E44"),sQuery(id+"F0.wireOp",EDGE,"E57")])]});
            fillet(context, id + "F2", {"entities" : qUnion([Q0, Q1, Q2, Q3, Q4, Q5, Q6, Q7, Q8, Q9, Q10, Q11, Q12, Q13, Q14, Q15, Q16]), "tangentPropagation" : true, "radius" : 25.4 * mm, "defaultsChanged" : true, "vertexSettings" : [], "allowEdgeOverflow" : false});
        }
    });
